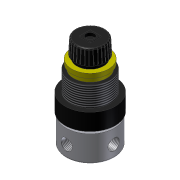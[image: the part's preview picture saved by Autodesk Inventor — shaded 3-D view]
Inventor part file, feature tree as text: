
AUTODESK INVENTOR PART (.ipt)
format: ipt  version: 2014 (Build 180170000, 170)  size: 624,640 bytes
history: native  units: mm (DEFAULTED — no unit token found)
features: extrude x12, sketch x12, projected_geometry x7, fillet x3, pattern_circular x2, thread x2, plane x1
ambient origin geometry x8: Origin, YZ Plane, XZ Plane, XY Plane, X Axis, Y Axis, Z Axis, Center Point
bodies: Solid1 (feature_tree)
feature tree (39):
  extrude  "Extrusion1"  Depth=19.5mm TaperAngle=0.0deg
  extrude  "Extrusion2"  Depth=2.0mm
  extrude  "Extrusion3"  Depth=30.0mm
  extrude  "Extrusion4"  Depth=25.0mm
  extrude  "Extrusion5"  Depth=27.5mm
  extrude  "Extrusion6"  Depth=20.0mm
  extrude  "Extrusion7"  Depth=23.0mm
  extrude  "Extrusion8"  Depth=1.0mm
  fillet  "Fillet1"  Radius=0.5mm
  extrude  "Extrusion9"  Depth=10.0mm TaperAngle=360.0deg
  fillet  "Fillet2"  Radius=10.0mm
  pattern_circular  "Circular Pattern1"  Count=4 Angle=360.0deg
  thread  "Thread1"  [1 undecoded]
  plane  "Work Plane1"
  extrude  "Extrusion10"  Depth=2.0mm TaperAngle=0.0deg
  thread  "Thread2"  [1 undecoded]
  pattern_circular  "Circular Pattern2"  [2 undecoded]
  fillet  "Fillet3"  [1 undecoded]
  extrude  "Extrusion11"  [1 undecoded]
  extrude  "Extrusion12"  [1 undecoded]
  sketch  "Sketch1"  dims[d0=36.0mm d1=19.5mm d2=0.0mm]
  sketch  "Sketch2"  dims[d3=2.0mm d4=0.0mm d5=37.5mm]
  sketch  "Sketch3"  dims[d6=12.5mm d7=0.0mm d8=30.0mm]
  projected_geometry  "Projected Loop1"
  sketch  "Sketch4"  dims[d9=15.0mm d10=0.0mm d11=25.0mm]
  sketch  "Sketch5"  dims[d12=3.3mm d13=0.0mm d14=27.5mm]
  projected_geometry  "Projected Loop2"
  sketch  "Sketch6"  dims[d15=3.3mm d16=0.0mm d17=20.0mm]
  projected_geometry  "Projected Loop3"
  sketch  "Sketch7"  dims[d18=3.0mm d19=0.0mm d20=23.0mm]
  projected_geometry  "Projected Loop4"
  sketch  "Sketch8"  dims[d21=11.0mm d22=-0.523599mm d23=1.0mm d24=0.5mm d25=0.0mm]
  projected_geometry  "Projected Loop5"
  sketch  "Sketch9"  dims[d26=0.15mm d27=300.0mm d29=360.0deg d30=10.0mm d31=0.0mm]
  sketch  "Sketch10"  dims[d32=9.75mm d33=0.0mm]
  projected_geometry  "Projected Loop6"
  sketch  "Sketch11"  dims[d34=10.0mm d35=0.0mm d36=8.5mm d37=40.0mm d39=360.0deg d40=1.0mm]
  sketch  "Sketch12"  dims[d41=6.3mm d42=2.0mm d43=0.0mm d44=0.5mm d45=0.0mm]
  projected_geometry  "Projected Loop7"
note: 7 required parameter values undecoded (feature->parameter linkage not recoverable at this tier; creation-order binding heuristic only, values carry confidence <= 0.55)
